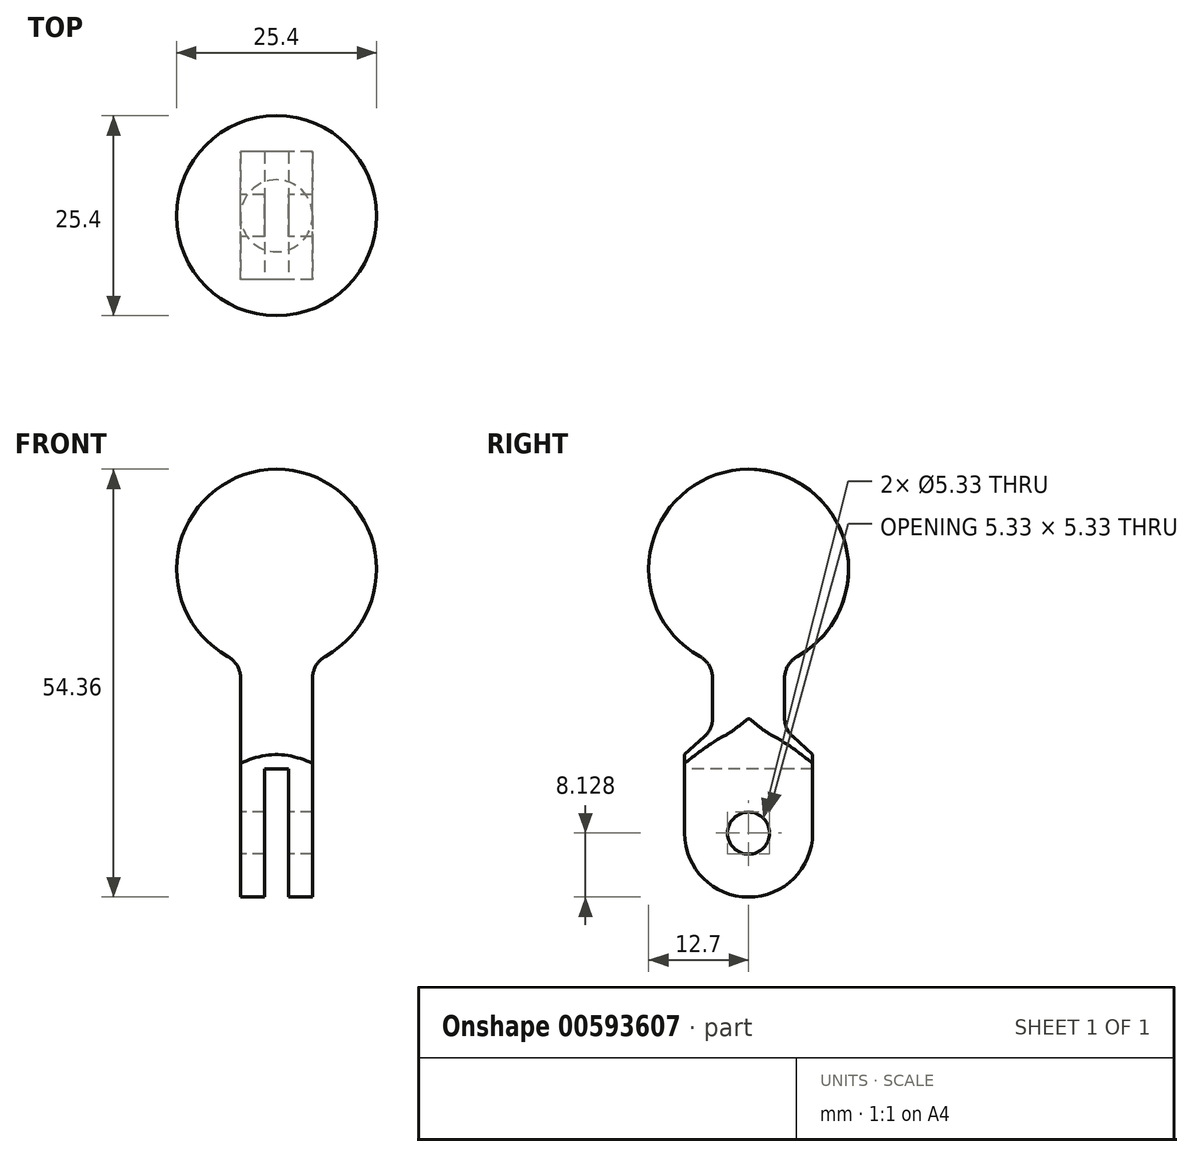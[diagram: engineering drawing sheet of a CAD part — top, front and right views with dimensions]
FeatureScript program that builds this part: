
annotation { "Feature Type Name" : "Feature", "Feature Type Description" : "" }
export const myFeature = defineFeature(function(context is Context, id is Id, definition is map)
    precondition{}
    {
        {
            var Q0;
            Q0=qCreatedBy(makeId("Front.planeOp"),FACE);
            var sketch = newSketch(context, id + "F0", { "sketchPlane" : qUnion([Q0])});
            skLineSegment(sketch, "E0", {"start": v(0, 16.26) * mm, "end": v(1.52, 16.26) * mm});
            skLineSegment(sketch, "E1", {"start": v(1.52, 16.26) * mm, "end": v(1.52, 0) * mm});
            skLineSegment(sketch, "E2", {"start": v(1.52, 0) * mm, "end": v(4.57, 0) * mm});
            skLineSegment(sketch, "E3", {"start": v(4.57, 0) * mm, "end": v(4.57, 16.26) * mm});
            skLineSegment(sketch, "E4", {"start": v(4.57, 16.26) * mm, "end": v(20.23, 16.26) * mm});
            skLineSegment(sketch, "E5", {"start": v(20.23, 16.26) * mm, "end": v(20.23, -12.13) * mm});
            skLineSegment(sketch, "E6", {"start": v(20.23, -12.13) * mm, "end": v(0, -12.13) * mm});
            skLineSegment(sketch, "E7", {"start": v(0, -12.13) * mm, "end": v(0, 16.26) * mm});
            skLineSegment(sketch, "E8.MirrorCS", {"start": v(0, 16.26) * mm, "end": v(-1.52, 16.26) * mm});
            skLineSegment(sketch, "E9.MirrorCS", {"start": v(-20.23, 16.26) * mm, "end": v(-20.23, -12.13) * mm});
            skLineSegment(sketch, "E10.MirrorCS", {"start": v(-1.52, 16.26) * mm, "end": v(-1.52, 0) * mm});
            skLineSegment(sketch, "E11.MirrorCS", {"start": v(-20.23, -12.13) * mm, "end": v(0, -12.13) * mm});
            skLineSegment(sketch, "E12.MirrorCS", {"start": v(-4.57, 0) * mm, "end": v(-4.57, 16.26) * mm});
            skLineSegment(sketch, "E13.MirrorCS", {"start": v(-1.52, 0) * mm, "end": v(-4.57, 0) * mm});
            skLineSegment(sketch, "E14.MirrorCS", {"start": v(-4.57, 16.26) * mm, "end": v(-20.23, 16.26) * mm});
            skSolve(sketch);
        }
        {
            var Q0;
            Q0=qCreatedBy(makeId("Right.planeOp"),FACE);
            var sketch = newSketch(context, id + "F1", { "sketchPlane" : qUnion([Q0])});
            skArc(sketch, "E15", {"start": v(-8.13, 8.13) * mm, "mid": v(0, 0) * mm, "end": v(8.13, 8.13) * mm});
            skCircle(sketch, "E16", {"center": v(0, 8.13) * mm, "radius": 2.67 * mm});
            skLineSegment(sketch, "E17", {"start": v(-8.13, 8.13) * mm, "end": v(-8.13, 16.26) * mm});
            skLineSegment(sketch, "E18", {"start": v(-8.13, 16.26) * mm, "end": v(8.13, 16.26) * mm});
            skLineSegment(sketch, "E19", {"start": v(8.13, 8.13) * mm, "end": v(8.13, 16.26) * mm});
            skSolve(sketch);
        }
        {
            var Q0;
            Q0=makeQuery(id+"F1.imprint","IMPRINT",FACE,{"disambiguationData":[TD([[makeQuery(id+"F1.imprint","IMPRINT",EDGE,{"derivedFrom":sQuery(id+"F1.wireOp",EDGE,"E15")}),1.0]])]});
            extrude(context, id + "F2", {"entities" : qUnion([Q0]), "endBound" : BoundingType.SYMMETRIC, "depth" : 12.7 * mm, "offsetDistance" : 25.4 * mm});
        }
        {
            var Q0;
            Q0=qCreatedBy(makeId("Right.planeOp"),FACE);
            var sketch = newSketch(context, id + "F3", { "sketchPlane" : qUnion([Q0])});
            skArc(sketch, "E20", {"start": v(6.2, 30.57) * mm, "mid": v(12.29, 44.86) * mm, "end": v(0, 54.36) * mm});
            skLineSegment(sketch, "E21", {"start": v(0, 54.36) * mm, "end": v(0, 16.26) * mm});
            skLineSegment(sketch, "E22", {"start": v(4.57, 27.8) * mm, "end": v(4.57, 22.74) * mm});
            skArc(sketch, "E23.filletArc", {"start": v(6.2, 30.57) * mm, "mid": v(5, 29.4) * mm, "end": v(4.57, 27.8) * mm});
            skLineSegment(sketch, "E24", {"start": v(0, 16.26) * mm, "end": v(10.16, 16.26) * mm});
            skLineSegment(sketch, "E25", {"start": v(10.16, 16.26) * mm, "end": v(5.61, 20.4) * mm});
            skPoint(sketch, "E26.visualSharp", {"position": v(4.57, 21.34) * mm});
            skArc(sketch, "E26.filletArc", {"start": v(4.57, 22.74) * mm, "mid": v(4.84, 21.46) * mm, "end": v(5.61, 20.4) * mm});
            skSolve(sketch);
        }
        {
            var Q0;
            Q0 = qSketchRegion(id + "F3", true);
            var Q1;
            Q1=sQuery(id+"F3.wireOp",EDGE,"E21");
            revolve(context, id + "F4", {"operationType" : NewBodyOperationType.ADD, "entities" : qUnion([Q0]), "axis" : qUnion([Q1]), "revolveType" : RevolveType.FULL});
        }
        {
            var Q0;
            Q0=makeQuery(id+"F0.imprint","IMPRINT",FACE,{"disambiguationData":[TD([[makeQuery(id+"F0.imprint","IMPRINT",EDGE,{"derivedFrom":sQuery(id+"F0.wireOp",EDGE,"E0")}),-1.0]])]});
            var Q1;
            Q1=makeQuery(id+"F0.imprint","IMPRINT",FACE,{"disambiguationData":[TD([[makeQuery(id+"F0.imprint","IMPRINT",EDGE,{"derivedFrom":sQuery(id+"F0.wireOp",EDGE,"E7")}),1.0]])]});
            extrude(context, id + "F5", {"entities" : qUnion([Q0, Q1]), "operationType" : NewBodyOperationType.REMOVE, "endBound" : BoundingType.SYMMETRIC, "oppositeDirection" : true, "depth" : 25.4 * mm, "offsetDistance" : 25.4 * mm});
        }
        {
            var Q0;
            {var subQ0=sQuery(id+"F1.wireOp",EDGE,"E18");var subQ2=sQuery(id+"F1.wireOp",EDGE,"E19");var subQ4=makeQuery(id+"F4.opRevolve","SWEPT_FACE",FACE,{"disambiguationData":[OSD([sQuery(id+"F3.wireOp",EDGE,"E24")])]});var subQ5=sQuery(id+"F1.wireOp",EDGE,"E17");var subQ6=sQuery(id+"F1.wireOp",EDGE,"E16");var subQ7=sQuery(id+"F1.wireOp",EDGE,"E15");Q0=makeQuery(id+"F5.boolean.opBoolean","MERGE",FACE,{"derivedFrom":[makeQuery(id+"F4.boolean.opBoolean","SPLIT",FACE,{"disambiguationData":[TD([makeQuery(id+"F2.opExtrude","CAP_FACE",FACE,{"disambiguationData":[OSD([subQ7,subQ6,subQ5,subQ0,subQ2])],"isStart":true})])],"derivedFrom":subQ4}),makeQuery(id+"F4.boolean.opBoolean","SPLIT",FACE,{"disambiguationData":[TD([makeQuery(id+"F2.opExtrude","CAP_FACE",FACE,{"disambiguationData":[OSD([subQ7,subQ6,subQ5,subQ0,subQ2])],"isStart":false})])],"derivedFrom":subQ4}),makeQuery(id+"F4.boolean.opBoolean","SPLIT",FACE,{"disambiguationData":[TD([makeQuery(id+"F2.opExtrude","SWEPT_FACE",FACE,{"disambiguationData":[OSD([subQ5])]})])],"derivedFrom":subQ4}),makeQuery(id+"F4.boolean.opBoolean","SPLIT",FACE,{"disambiguationData":[TD([makeQuery(id+"F2.opExtrude","SWEPT_FACE",FACE,{"disambiguationData":[OSD([subQ2])]})])],"derivedFrom":subQ4}),makeQuery(id+"F5.opExtrude","SWEPT_FACE",FACE,{"disambiguationData":[OSD([sQuery(id+"F0.wireOp",EDGE,"E0"),sQuery(id+"F0.wireOp",EDGE,"E8.MirrorCS")])]}),makeQuery(id+"F5.opExtrude","SWEPT_FACE",FACE,{"disambiguationData":[OSD([sQuery(id+"F0.wireOp",EDGE,"E4")])]}),makeQuery(id+"F5.opExtrude","SWEPT_FACE",FACE,{"disambiguationData":[OSD([sQuery(id+"F0.wireOp",EDGE,"E14.MirrorCS")])]})]});}
            var sketch = newSketch(context, id + "F6", { "sketchPlane" : qUnion([Q0])});
            skLineSegment(sketch, "E27.bottom", {"start": v(-4.57, 8.13) * mm, "end": v(4.57, 8.13) * mm});
            skLineSegment(sketch, "E27.top", {"start": v(-4.57, -8.13) * mm, "end": v(4.57, -8.13) * mm});
            skLineSegment(sketch, "E27.left", {"start": v(-4.57, 8.13) * mm, "end": v(-4.57, -8.13) * mm});
            skLineSegment(sketch, "E27.right", {"start": v(4.57, 8.13) * mm, "end": v(4.57, -8.13) * mm});
            skLineSegment(sketch, "E28.bottom", {"start": v(-17, 17) * mm, "end": v(15.79, 17) * mm});
            skLineSegment(sketch, "E28.top", {"start": v(-17, -18.56) * mm, "end": v(15.79, -18.56) * mm});
            skLineSegment(sketch, "E28.left", {"start": v(-17, 17) * mm, "end": v(-17, -18.56) * mm});
            skLineSegment(sketch, "E28.right", {"start": v(15.79, 17) * mm, "end": v(15.79, -18.56) * mm});
            skSolve(sketch);
        }
        {
            var Q0;
            Q0=makeQuery(id+"F6.imprint","IMPRINT",FACE,{"disambiguationData":[TD([[makeQuery(id+"F6.imprint","IMPRINT",EDGE,{"derivedFrom":sQuery(id+"F6.wireOp",EDGE,"E28.bottom")}),-1.0]])]});
            var Q1;
            {var subQ7=sQuery(id+"F6.wireOp",EDGE,"E27.left");Q1=makeQuery(id+"F6.imprint","IMPRINT",FACE,{"disambiguationData":[TD([[makeQuery(id+"F6.imprint","IMPRINT",EDGE,{"derivedFrom":subQ7}),1.0]])]});}
            extrude(context, id + "F7", {"entities" : qUnion([Q0, Q1]), "operationType" : NewBodyOperationType.REMOVE, "oppositeDirection" : true, "depth" : 6.35 * mm, "offsetDistance" : 25.4 * mm});
        }
    });
